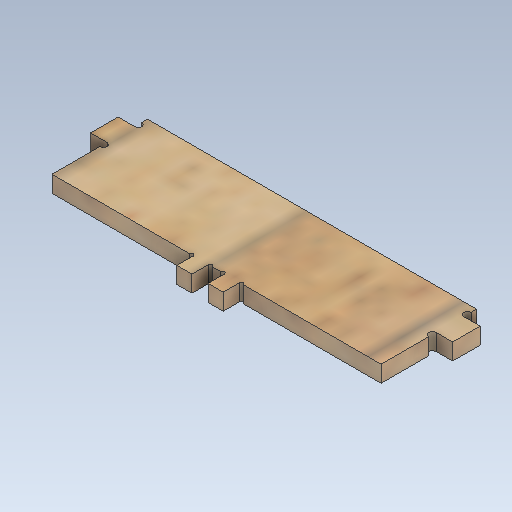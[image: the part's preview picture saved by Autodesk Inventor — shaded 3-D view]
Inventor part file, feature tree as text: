
AUTODESK INVENTOR PART (.ipt)
format: ipt  version: 2020 (Build 240168000, 168)  size: 205,824 bytes
history: native  units: mm
features: extrude x2, sketch x2
ambient origin geometry x8: Origin, YZ Plane, XZ Plane, XY Plane, X Axis, Y Axis, Z Axis, Center Point
bodies: Solid1 (feature_tree)
feature tree (4):
  extrude  "Extrusion1"  Depth=2.666667mm
  extrude  "Extrusion2"  Depth=1.333333mm
  sketch  "Sketch1"  dims[d1=2.0mm d2=2.666667mm]
  sketch  "Sketch2"  dims[d5=2.666667mm d6=17.333333mm d9=6.0mm d10=119.5mm d11=10.0mm d18=44.0mm d19=44.0mm d21=20.0mm d23=6.0mm d24=6.0mm d25=0.0mm d26=6.0mm d28=6.0mm d29=6.0mm d35=0.0mm d36=0.0mm d37=1.333333mm d38=1.333333mm d39=1.333333mm d40=1.333333mm]
